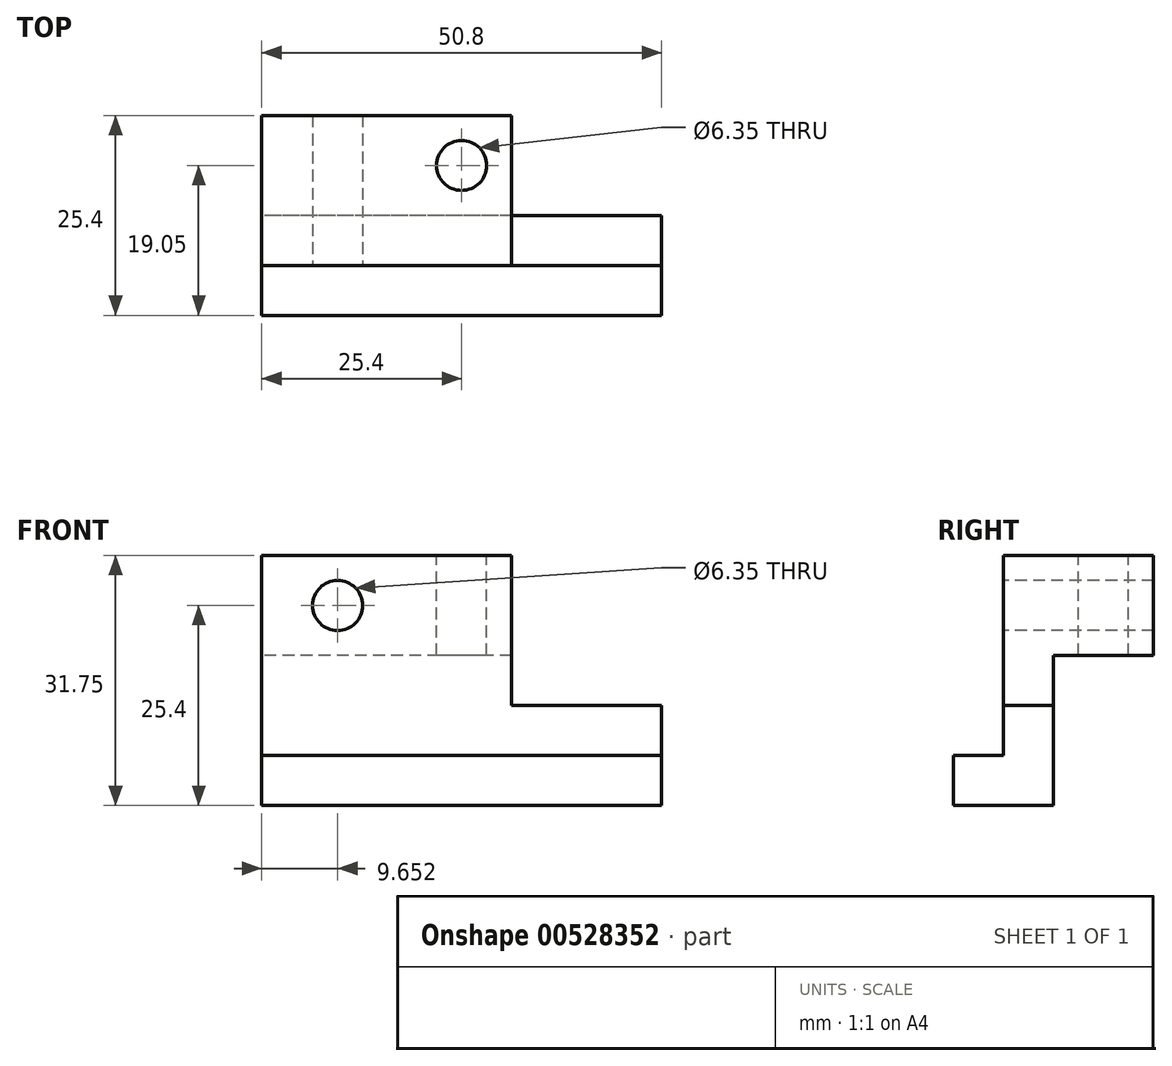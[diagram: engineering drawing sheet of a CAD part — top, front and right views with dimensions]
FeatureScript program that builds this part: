
annotation { "Feature Type Name" : "Feature", "Feature Type Description" : "" }
export const myFeature = defineFeature(function(context is Context, id is Id, definition is map)
    precondition{}
    {
        {
            var Q0;
            Q0=qCreatedBy(makeId("Front.planeOp"),FACE);
            var sketch = newSketch(context, id + "F0", { "sketchPlane" : qUnion([Q0])});
            skLineSegment(sketch, "E0.bottom", {"start": v(0, 0) * mm, "end": v(-50.8, 0) * mm});
            skLineSegment(sketch, "E0.top", {"start": v(-19.05, 31.75) * mm, "end": v(-50.8, 31.75) * mm});
            skLineSegment(sketch, "E0.left", {"start": v(0, 0) * mm, "end": v(0, 12.7) * mm});
            skLineSegment(sketch, "E0.right", {"start": v(-50.8, 0) * mm, "end": v(-50.8, 31.75) * mm});
            skLineSegment(sketch, "E1", {"start": v(-50.8, 6.35) * mm, "end": v(0, 6.35) * mm});
            skLineSegment(sketch, "E2", {"start": v(-19.05, 31.75) * mm, "end": v(-19.05, 12.7) * mm});
            skLineSegment(sketch, "E3", {"start": v(-19.05, 12.7) * mm, "end": v(0, 12.7) * mm});
            skLineSegment(sketch, "E4", {"start": v(0, 12.7) * mm, "end": v(-19.05, 12.7) * mm});
            skLineSegment(sketch, "E5", {"start": v(-19.05, 19.05) * mm, "end": v(-50.8, 19.05) * mm});
            skPoint(sketch, "E5.endSnap0", {"position": v(-50.8, 15.88) * mm});
            skCircle(sketch, "E6", {"center": v(-41.15, 25.4) * mm, "radius": 3.18 * mm});
            skSolve(sketch);
        }
        {
            var Q0;
            {var subQ0=sQuery(id+"F0.wireOp",EDGE,"E0.bottom");Q0=makeQuery(id+"F0.imprint","IMPRINT",FACE,{"disambiguationData":[TD([[makeQuery(id+"F0.imprint","IMPRINT",EDGE,{"derivedFrom":subQ0}),-1.0]])]});}
            extrude(context, id + "F1", {"entities" : qUnion([Q0]), "depth" : 6.35 * mm, "offsetDistance" : 25.4 * mm});
        }
        {
            var Q0;
            {var subQ3=sQuery(id+"F0.wireOp",EDGE,"E1");Q0=makeQuery(id+"F0.imprint","IMPRINT",FACE,{"disambiguationData":[TD([[makeQuery(id+"F0.imprint","IMPRINT",EDGE,{"derivedFrom":subQ3}),1.0]])]});}
            var Q1;
            {var subQ0=sQuery(id+"F0.wireOp",EDGE,"E0.bottom");Q1=makeQuery(id+"F0.imprint","IMPRINT",FACE,{"disambiguationData":[TD([[makeQuery(id+"F0.imprint","IMPRINT",EDGE,{"derivedFrom":subQ0}),-1.0]])]});}
            extrude(context, id + "F2", {"entities" : qUnion([Q0, Q1]), "operationType" : NewBodyOperationType.ADD, "oppositeDirection" : true, "depth" : 6.35 * mm, "offsetDistance" : 25.4 * mm});
        }
        {
            var Q0;
            {var subQ1=sQuery(id+"F0.wireOp",EDGE,"E0.top");Q0=makeQuery(id+"F0.imprint","IMPRINT",FACE,{"disambiguationData":[TD([[makeQuery(id+"F0.imprint","IMPRINT",EDGE,{"derivedFrom":subQ1}),1.0]])]});}
            extrude(context, id + "F3", {"entities" : qUnion([Q0]), "operationType" : NewBodyOperationType.ADD, "oppositeDirection" : true, "depth" : 19.05 * mm, "offsetDistance" : 25.4 * mm});
        }
        {
            var Q0;
            Q0=makeQuery(id+"F3.opExtrude","SWEPT_FACE",FACE,{"disambiguationData":[OSD([sQuery(id+"F0.wireOp",EDGE,"E0.top")])]});
            var sketch = newSketch(context, id + "F4", { "sketchPlane" : qUnion([Q0])});
            skCircle(sketch, "E7", {"center": v(-25.4, 12.7) * mm, "radius": 3.18 * mm});
            skSolve(sketch);
        }
        {
            var Q0;
            Q0=makeQuery(id+"F4.imprint","IMPRINT",FACE,{"disambiguationData":[TD([[makeQuery(id+"F4.imprint","IMPRINT",EDGE,{"derivedFrom":sQuery(id+"F4.wireOp",EDGE,"E7")}),1.0]])]});
            extrude(context, id + "F5", {"entities" : qUnion([Q0]), "operationType" : NewBodyOperationType.REMOVE, "endBound" : BoundingType.THROUGH_ALL, "oppositeDirection" : true, "depth" : 25.4 * mm, "offsetDistance" : 25.4 * mm});
        }
    });
